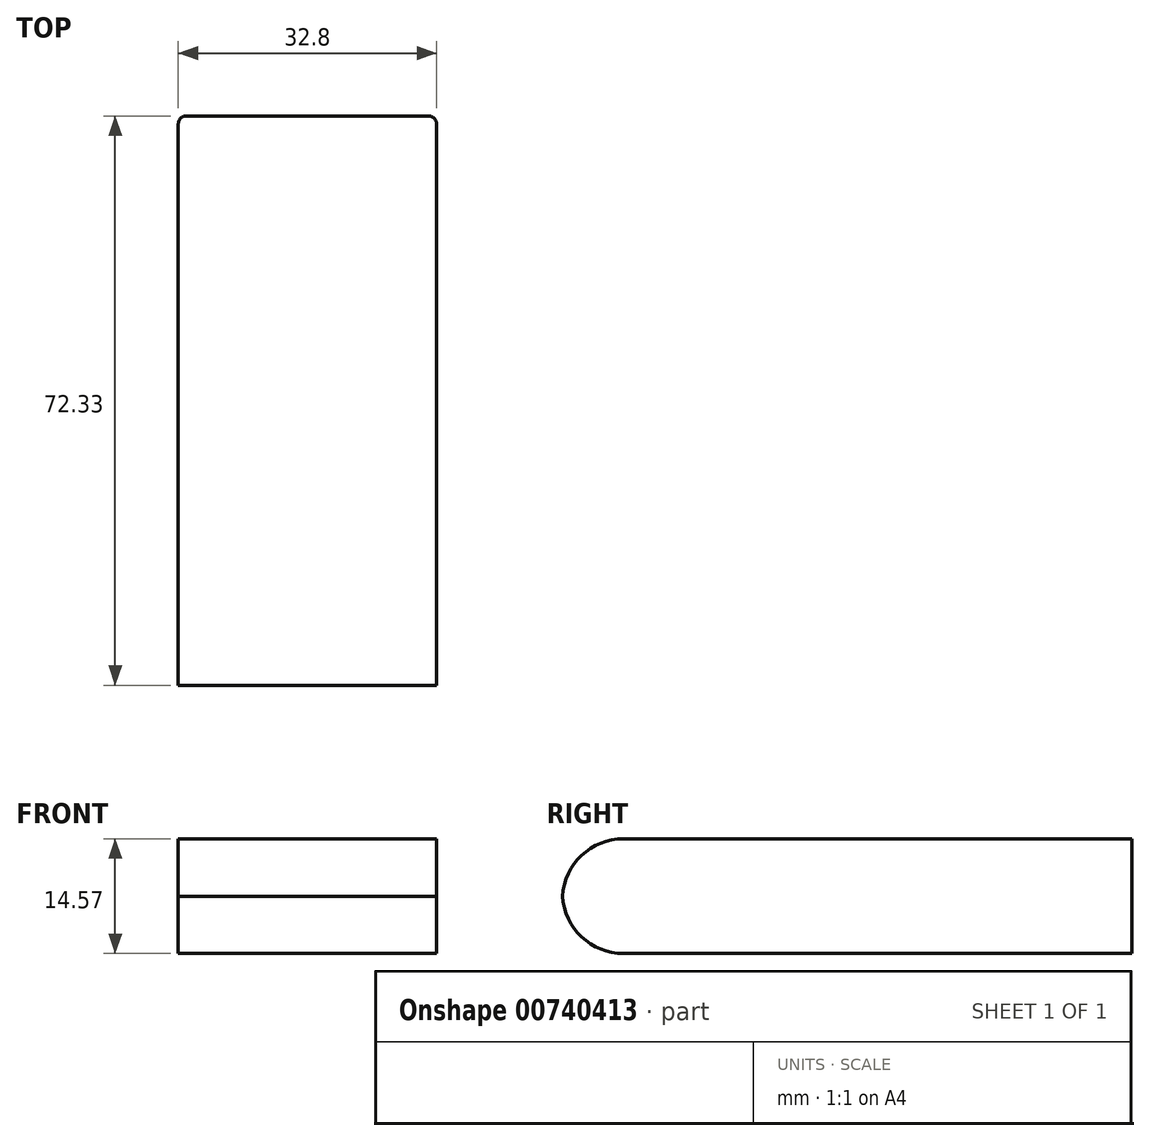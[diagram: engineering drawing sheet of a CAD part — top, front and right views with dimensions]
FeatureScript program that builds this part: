
annotation { "Feature Type Name" : "Feature", "Feature Type Description" : "" }
export const myFeature = defineFeature(function(context is Context, id is Id, definition is map)
    precondition{}
    {
        {
            var Q0;
            Q0=qCreatedBy(makeId("Front.planeOp"),FACE);
            var sketch = newSketch(context, id + "F0", { "sketchPlane" : qUnion([Q0])});
            skLineSegment(sketch, "E0.bottom", {"start": v(0, 0) * mm, "end": v(32.8, 0) * mm});
            skLineSegment(sketch, "E0.top", {"start": v(0, 14.57) * mm, "end": v(32.8, 14.57) * mm});
            skLineSegment(sketch, "E0.left", {"start": v(0, 0) * mm, "end": v(0, 14.57) * mm});
            skLineSegment(sketch, "E0.right", {"start": v(32.8, 0) * mm, "end": v(32.8, 14.57) * mm});
            skSolve(sketch);
        }
        {
            var Q0;
            Q0=qSketchRegion(id+"F0",true);
            extrude(context, id + "F1", {"entities" : qUnion([Q0]), "depth" : 72.34 * mm, "offsetDistance" : 25 * mm});
        }
        {
            var Q0;
            Q0=makeQuery(id+"F1.opExtrude","CAP_EDGE",EDGE,{"disambiguationData":[OSD([sQuery(id+"F0.wireOp",EDGE,"E0.top")])],"isStart":false});
            var Q1;
            Q1=makeQuery(id+"F1.opExtrude","CAP_EDGE",EDGE,{"disambiguationData":[OSD([sQuery(id+"F0.wireOp",EDGE,"E0.bottom")])],"isStart":false});
            fillet(context, id + "F2", {"entities" : qUnion([Q0, Q1]), "radius" : 7.75 * mm, "tangentPropagation" : true, "allowEdgeOverflow" : false});
        }
        {
            var Q0;
            Q0=makeQuery(id+"F1.opExtrude","CAP_EDGE",EDGE,{"disambiguationData":[OSD([sQuery(id+"F0.wireOp",EDGE,"E0.left")])],"isStart":true});
            var Q1;
            Q1=makeQuery(id+"F1.opExtrude","CAP_EDGE",EDGE,{"disambiguationData":[OSD([sQuery(id+"F0.wireOp",EDGE,"E0.right")])],"isStart":true});
            fillet(context, id + "F3", {"entities" : qUnion([Q0, Q1]), "radius" : 1 * mm, "tangentPropagation" : true, "allowEdgeOverflow" : false});
        }
    });
